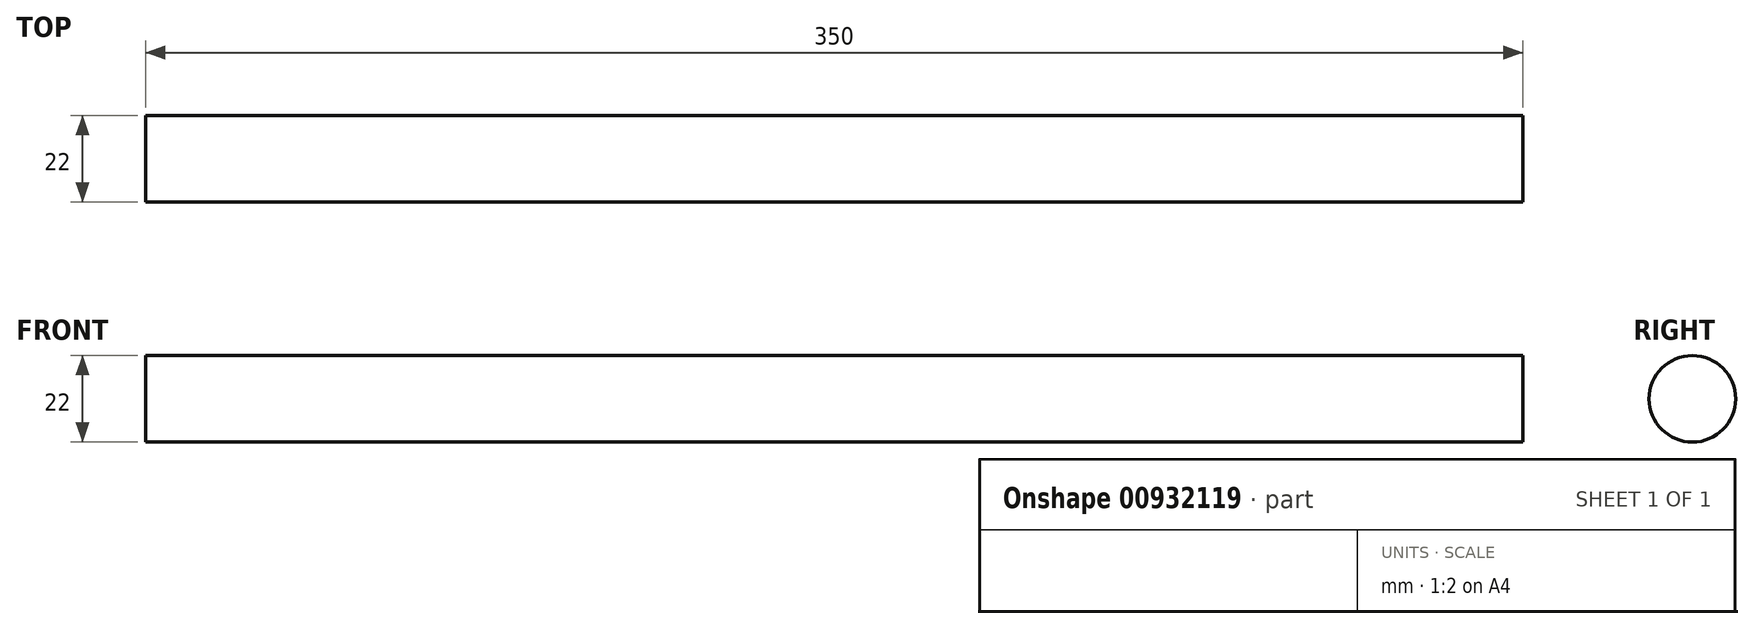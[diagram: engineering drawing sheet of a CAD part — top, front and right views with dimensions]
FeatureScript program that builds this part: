
annotation { "Feature Type Name" : "Feature", "Feature Type Description" : "" }
export const myFeature = defineFeature(function(context is Context, id is Id, definition is map)
    precondition{}
    {
        {
            var Q0;
            Q0=qCreatedBy(makeId("Right.planeOp"),FACE);
            var sketch = newSketch(context, id + "F0", { "sketchPlane" : qUnion([Q0])});
            skCircle(sketch, "E0", {"center": v(0, 0) * mm, "radius": 11 * mm});
            skSolve(sketch);
        }
        {
            var Q0;
            Q0=makeQuery(id+"F0.imprint","IMPRINT",FACE,{"disambiguationData":[TD([[makeQuery(id+"F0.imprint","IMPRINT",EDGE,{"derivedFrom":sQuery(id+"F0.wireOp",EDGE,"E0")}),1.0]])]});
            extrude(context, id + "F1", {"entities" : qUnion([Q0]), "depth" : 350 * mm, "offsetDistance" : 25 * mm});
        }
    });
